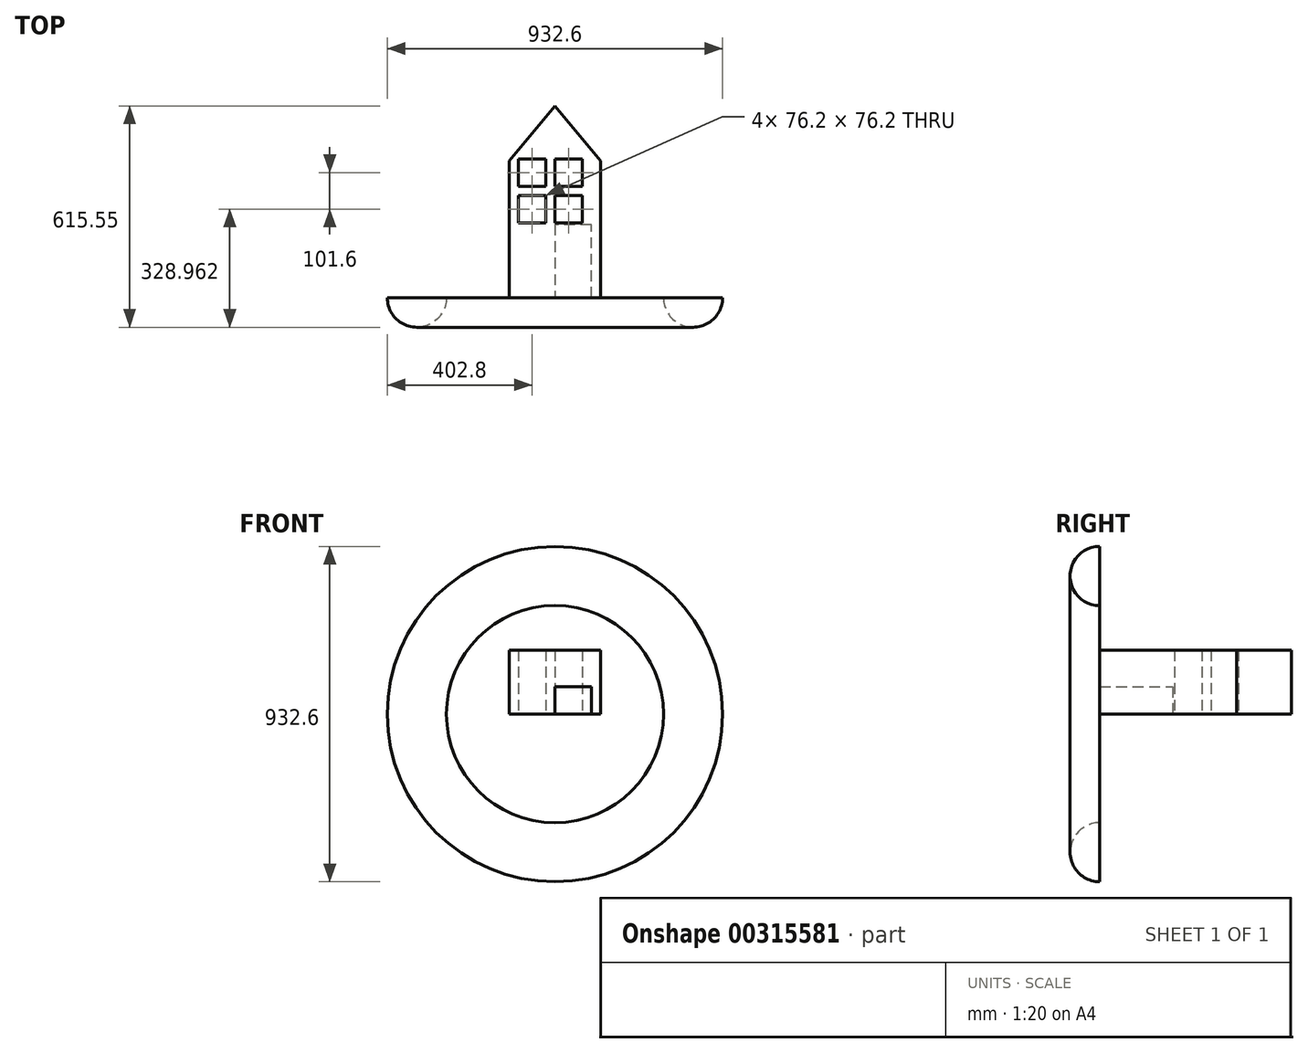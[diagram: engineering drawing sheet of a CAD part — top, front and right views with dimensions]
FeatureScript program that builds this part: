
annotation { "Feature Type Name" : "Feature", "Feature Type Description" : "" }
export const myFeature = defineFeature(function(context is Context, id is Id, definition is map)
    precondition{}
    {
        {
            var Q0;
            Q0=qCreatedBy(makeId("Top.planeOp"),FACE);
            var sketch = newSketch(context, id + "F0", { "sketchPlane" : qUnion([Q0])});
            skLineSegment(sketch, "E0.bottom", {"start": v(-127, 190.5) * mm, "end": v(127, 190.5) * mm});
            skLineSegment(sketch, "E0.top", {"start": v(-127, -190.5) * mm, "end": v(127, -190.5) * mm});
            skLineSegment(sketch, "E0.left", {"start": v(-127, 190.5) * mm, "end": v(-127, -190.5) * mm});
            skLineSegment(sketch, "E0.right", {"start": v(127, 190.5) * mm, "end": v(127, -190.5) * mm});
            skPoint(sketch, "E0.middle", {"position": v(0, 0) * mm});
            skLineSegment(sketch, "E1", {"start": v(-127, 190.5) * mm, "end": v(0, 342.9) * mm});
            skLineSegment(sketch, "E2", {"start": v(0, 342.9) * mm, "end": v(127, 190.5) * mm});
            skSolve(sketch);
        }
        {
            var Q0;
            Q0=makeQuery(id+"F0.imprint","IMPRINT",FACE,{"disambiguationData":[TD([[makeQuery(id+"F0.imprint","IMPRINT",EDGE,{"derivedFrom":sQuery(id+"F0.wireOp",EDGE,"E0.bottom")}),1.0]])]});
            var Q1;
            Q1=makeQuery(id+"F0.imprint","IMPRINT",FACE,{"disambiguationData":[TD([[makeQuery(id+"F0.imprint","IMPRINT",EDGE,{"derivedFrom":sQuery(id+"F0.wireOp",EDGE,"E0.bottom")}),-1.0]])]});
            extrude(context, id + "F1", {"entities" : qUnion([Q0, Q1]), "depth" : 177.8 * mm});
        }
        {
            var Q0;
            Q0=makeQuery(id+"F1.opExtrude","CAP_FACE",FACE,{"disambiguationData":[OSD([sQuery(id+"F0.wireOp",EDGE,"E0.top"),sQuery(id+"F0.wireOp",EDGE,"E0.left"),sQuery(id+"F0.wireOp",EDGE,"E0.right"),sQuery(id+"F0.wireOp",EDGE,"E1"),sQuery(id+"F0.wireOp",EDGE,"E2")])],"isStart":true});
            var sketch = newSketch(context, id + "F2", { "sketchPlane" : qUnion([Q0])});
            skLineSegment(sketch, "E3", {"start": v(101.6, 190.5) * mm, "end": v(101.6, -12.7) * mm});
            skLineSegment(sketch, "E4", {"start": v(101.6, -12.7) * mm, "end": v(0, -12.7) * mm});
            skLineSegment(sketch, "E5", {"start": v(0, -12.7) * mm, "end": v(0, 190.5) * mm});
            skSolve(sketch);
        }
        {
            var Q0;
            {var subQ0=sQuery(id+"F2.wireOp",EDGE,"E3");Q0=makeQuery(id+"F2.imprint","IMPRINT",FACE,{"disambiguationData":[TD([[makeQuery(id+"F2.imprint","IMPRINT",EDGE,{"derivedFrom":subQ0}),-1.0]])]});}
            extrude(context, id + "F3", {"entities" : qUnion([Q0]), "operationType" : NewBodyOperationType.REMOVE, "oppositeDirection" : true, "depth" : 76.2 * mm});
        }
        {
            var Q0;
            Q0=qCreatedBy(makeId("Top.planeOp"),FACE);
            var sketch = newSketch(context, id + "F4", { "sketchPlane" : qUnion([Q0])});
            skLineSegment(sketch, "E6.0.0", {"start": v(101.6, 12.7) * mm, "end": v(0, 12.7) * mm});
            skLineSegment(sketch, "E6.0.1", {"start": v(0, 12.7) * mm, "end": v(0, -190.5) * mm});
            skLineSegment(sketch, "E6.0.2", {"start": v(0, -190.5) * mm, "end": v(-127, -190.5) * mm});
            skLineSegment(sketch, "E6.0.3", {"start": v(-127, -190.5) * mm, "end": v(-127, 190.5) * mm});
            skLineSegment(sketch, "E6.0.4", {"start": v(-127, 190.5) * mm, "end": v(0, 342.9) * mm});
            skLineSegment(sketch, "E6.0.5", {"start": v(0, 342.9) * mm, "end": v(127, 190.5) * mm});
            skLineSegment(sketch, "E6.0.6", {"start": v(127, 190.5) * mm, "end": v(127, -190.5) * mm});
            skLineSegment(sketch, "E6.0.7", {"start": v(127, -190.5) * mm, "end": v(101.6, -190.5) * mm});
            skLineSegment(sketch, "E6.0.8", {"start": v(101.6, -190.5) * mm, "end": v(101.6, 12.7) * mm});
            skArc(sketch, "E7", {"start": v(302, -190.5) * mm, "mid": v(384.15, -272.65) * mm, "end": v(466.3, -190.5) * mm});
            skLineSegment(sketch, "E8", {"start": v(466.3, -190.5) * mm, "end": v(302, -190.5) * mm});
            skLineSegment(sketch, "E9", {"start": v(0, 342.9) * mm, "end": v(0, -368.92) * mm, "construction": true});
            skSolve(sketch);
        }
        {
            var Q0;
            Q0=makeQuery(id+"F4.imprint","IMPRINT",FACE,{"disambiguationData":[TD([[makeQuery(id+"F4.imprint","IMPRINT",EDGE,{"derivedFrom":sQuery(id+"F4.wireOp",EDGE,"E7")}),1.0]])]});
            var Q1;
            Q1=sQuery(id+"F4.wireOp",EDGE,"E9");
            revolve(context, id + "F5", {"entities" : qUnion([Q0]), "axis" : qUnion([Q1]), "revolveType" : RevolveType.FULL});
        }
        {
            var Q0;
            Q0=makeQuery(id+"F1.opExtrude","CAP_FACE",FACE,{"disambiguationData":[OSD([sQuery(id+"F0.wireOp",EDGE,"E0.top"),sQuery(id+"F0.wireOp",EDGE,"E0.left"),sQuery(id+"F0.wireOp",EDGE,"E0.right"),sQuery(id+"F0.wireOp",EDGE,"E1"),sQuery(id+"F0.wireOp",EDGE,"E2")])],"isStart":true});
            var sketch = newSketch(context, id + "F6", { "sketchPlane" : qUnion([Q0])});
            skLineSegment(sketch, "E10.bottom", {"start": v(76.2, -94.41) * mm, "end": v(0, -94.41) * mm});
            skLineSegment(sketch, "E10.top", {"start": v(76.2, -18.21) * mm, "end": v(0, -18.21) * mm});
            skLineSegment(sketch, "E10.left", {"start": v(76.2, -94.41) * mm, "end": v(76.2, -18.21) * mm});
            skLineSegment(sketch, "E10.right", {"start": v(0, -94.41) * mm, "end": v(0, -18.21) * mm});
            skLineSegment(sketch, "E11.0.1.0", {"start": v(76.2, -196.01) * mm, "end": v(0, -196.01) * mm});
            skLineSegment(sketch, "E11.0.1.1", {"start": v(76.2, -196.01) * mm, "end": v(76.2, -119.81) * mm});
            skLineSegment(sketch, "E11.0.1.2", {"start": v(76.2, -119.81) * mm, "end": v(0, -119.81) * mm});
            skLineSegment(sketch, "E11.0.1.3", {"start": v(0, -196.01) * mm, "end": v(0, -119.81) * mm});
            skLineSegment(sketch, "E11.1.0.0", {"start": v(-25.4, -94.41) * mm, "end": v(-101.6, -94.41) * mm});
            skLineSegment(sketch, "E11.1.0.1", {"start": v(-25.4, -94.41) * mm, "end": v(-25.4, -18.21) * mm});
            skLineSegment(sketch, "E11.1.0.2", {"start": v(-25.4, -18.21) * mm, "end": v(-101.6, -18.21) * mm});
            skLineSegment(sketch, "E11.1.0.3", {"start": v(-101.6, -94.41) * mm, "end": v(-101.6, -18.21) * mm});
            skLineSegment(sketch, "E11.1.1.0", {"start": v(-25.4, -196.01) * mm, "end": v(-101.6, -196.01) * mm});
            skLineSegment(sketch, "E11.1.1.1", {"start": v(-25.4, -196.01) * mm, "end": v(-25.4, -119.81) * mm});
            skLineSegment(sketch, "E11.1.1.2", {"start": v(-25.4, -119.81) * mm, "end": v(-101.6, -119.81) * mm});
            skLineSegment(sketch, "E11.1.1.3", {"start": v(-101.6, -196.01) * mm, "end": v(-101.6, -119.81) * mm});
            skLineSegment(sketch, "E11.direction1", {"start": v(0, -94.41) * mm, "end": v(-101.6, -94.41) * mm, "construction": true});
            skLineSegment(sketch, "E11.direction2", {"start": v(0, -94.41) * mm, "end": v(0, -196.01) * mm, "construction": true});
            skSolve(sketch);
        }
        {
            var Q0;
            Q0=makeQuery(id+"F6.imprint","IMPRINT",FACE,{"disambiguationData":[TD([[makeQuery(id+"F6.imprint","IMPRINT",EDGE,{"derivedFrom":sQuery(id+"F6.wireOp",EDGE,"E11.0.1.0")}),-1.0]])]});
            var Q1;
            Q1=makeQuery(id+"F6.imprint","IMPRINT",FACE,{"disambiguationData":[TD([[makeQuery(id+"F6.imprint","IMPRINT",EDGE,{"derivedFrom":sQuery(id+"F6.wireOp",EDGE,"E10.bottom")}),-1.0]])]});
            var Q2;
            Q2=makeQuery(id+"F6.imprint","IMPRINT",FACE,{"disambiguationData":[TD([[makeQuery(id+"F6.imprint","IMPRINT",EDGE,{"derivedFrom":sQuery(id+"F6.wireOp",EDGE,"E11.1.0.0")}),-1.0]])]});
            var Q3;
            Q3=makeQuery(id+"F6.imprint","IMPRINT",FACE,{"disambiguationData":[TD([[makeQuery(id+"F6.imprint","IMPRINT",EDGE,{"derivedFrom":sQuery(id+"F6.wireOp",EDGE,"E11.1.1.0")}),-1.0]])]});
            var Q4;
            Q4=makeQuery(id+"F1.opExtrude","CAP_FACE",FACE,{"disambiguationData":[OSD([sQuery(id+"F0.wireOp",EDGE,"E0.top"),sQuery(id+"F0.wireOp",EDGE,"E0.left"),sQuery(id+"F0.wireOp",EDGE,"E0.right"),sQuery(id+"F0.wireOp",EDGE,"E1"),sQuery(id+"F0.wireOp",EDGE,"E2")])],"isStart":false});
            extrude(context, id + "F7", {"entities" : qUnion([Q0, Q1, Q2, Q3]), "operationType" : NewBodyOperationType.REMOVE, "endBound" : BoundingType.UP_TO_SURFACE, "oppositeDirection" : true, "endBoundEntityFace" : qUnion([Q4]), "depth" : 203.2 * mm});
        }
    });
